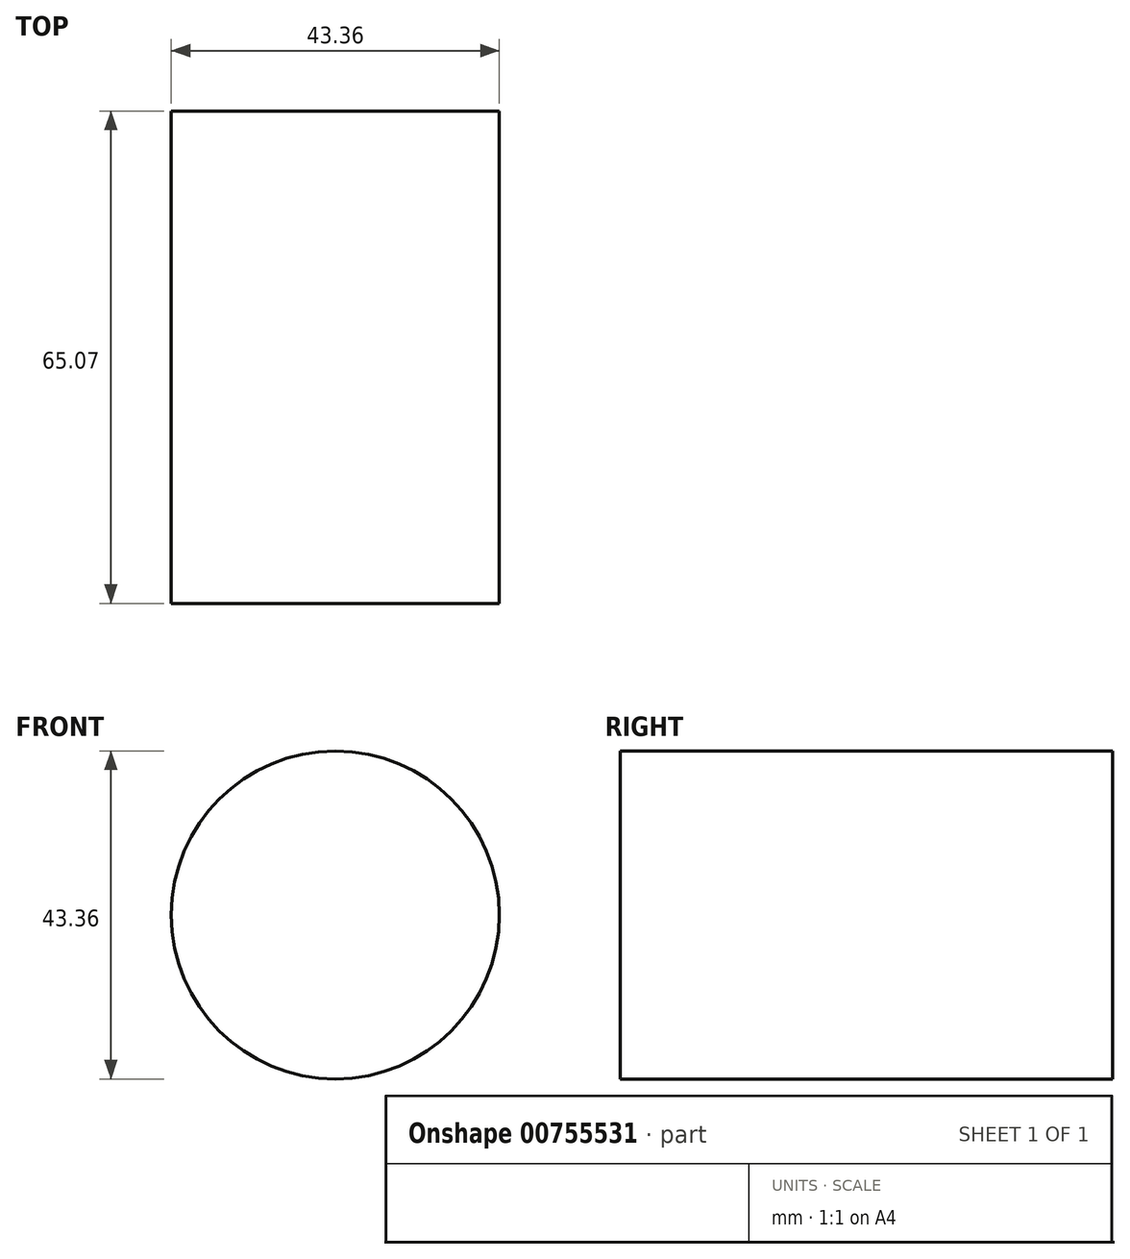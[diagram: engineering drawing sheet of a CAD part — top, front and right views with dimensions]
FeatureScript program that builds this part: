
annotation { "Feature Type Name" : "Feature", "Feature Type Description" : "" }
export const myFeature = defineFeature(function(context is Context, id is Id, definition is map)
    precondition{}
    {
        {
            var Q0;
            Q0=qCreatedBy(makeId("Front.planeOp"),FACE);
            var sketch = newSketch(context, id + "F0", { "sketchPlane" : qUnion([Q0])});
            skCircle(sketch, "E0", {"center": v(0, 0) * mm, "radius": 21.68 * mm});
            skSolve(sketch);
        }
        {
            var Q0;
            Q0=makeQuery(id+"F0.imprint","IMPRINT",FACE,{"disambiguationData":[TD([[makeQuery(id+"F0.imprint","IMPRINT",EDGE,{"derivedFrom":sQuery(id+"F0.wireOp",EDGE,"E0")}),1.0]])]});
            extrude(context, id + "F1", {"entities" : qUnion([Q0]), "oppositeDirection" : true, "depth" : 65.07 * mm, "offsetDistance" : 25.4 * mm});
        }
    });
